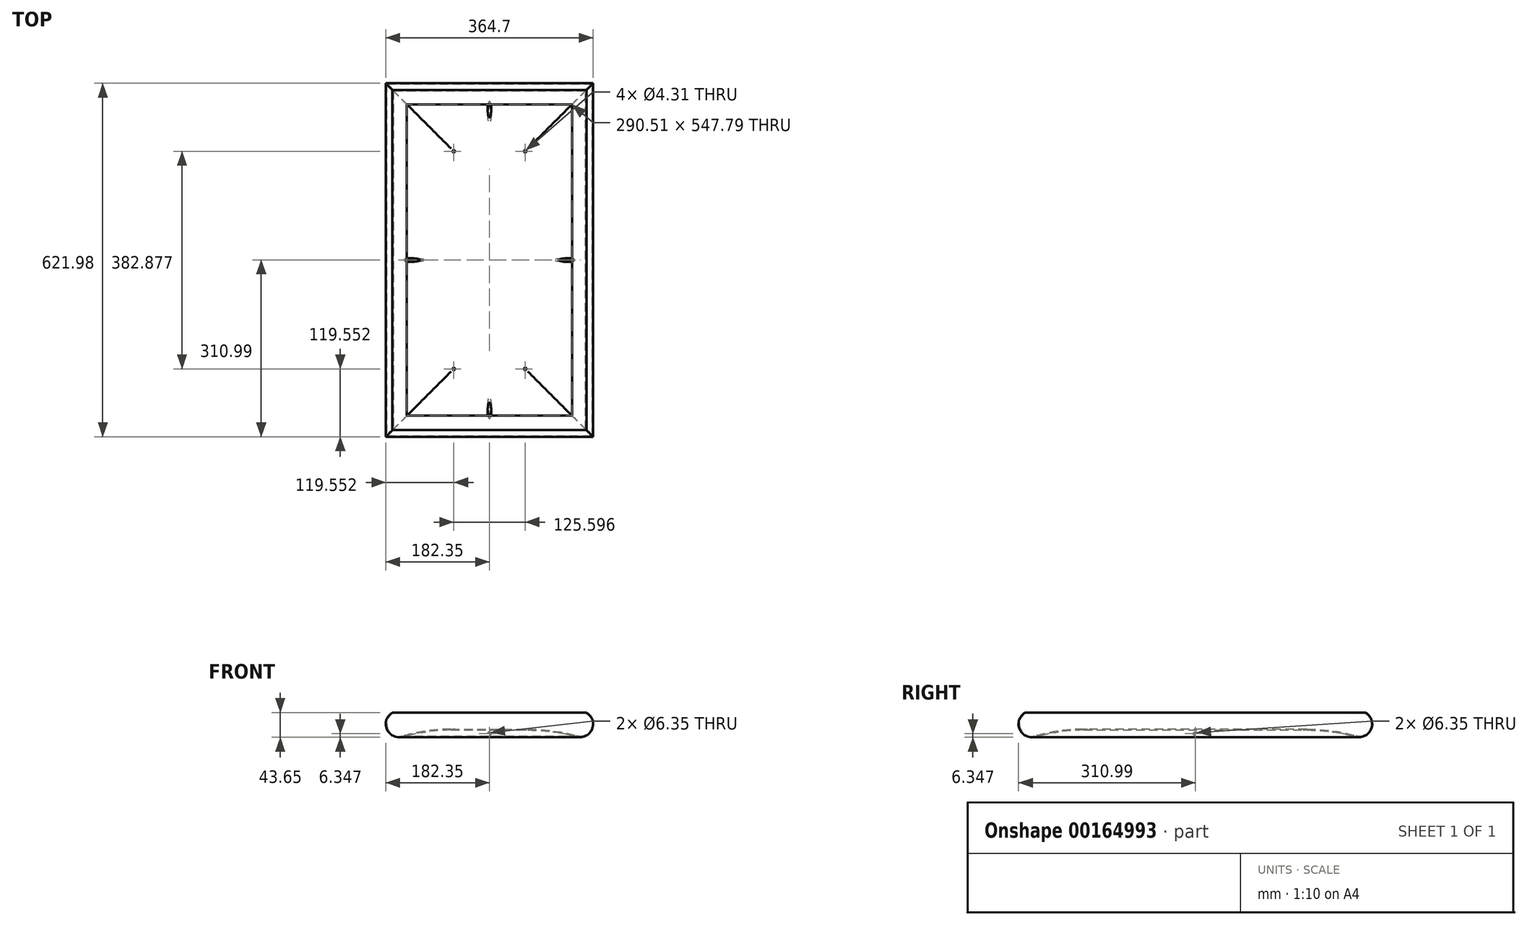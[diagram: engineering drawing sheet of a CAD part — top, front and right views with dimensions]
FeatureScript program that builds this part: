
annotation { "Feature Type Name" : "Feature", "Feature Type Description" : "" }
export const myFeature = defineFeature(function(context is Context, id is Id, definition is map)
    precondition{}
    {
        {
            var Q0;
            Q0=qCreatedBy(makeId("Top.planeOp"),FACE);
            var sketch = newSketch(context, id + "F0", { "sketchPlane" : qUnion([Q0])});
            skLineSegment(sketch, "E0.bottom", {"start": v(170.66, 299.3) * mm, "end": v(-170.66, 299.3) * mm});
            skLineSegment(sketch, "E0.top", {"start": v(170.66, -299.3) * mm, "end": v(-170.66, -299.3) * mm});
            skLineSegment(sketch, "E0.left", {"start": v(170.66, 299.3) * mm, "end": v(170.66, -299.3) * mm});
            skLineSegment(sketch, "E0.right", {"start": v(-170.66, 299.3) * mm, "end": v(-170.66, -299.3) * mm});
            skPoint(sketch, "E0.middle", {"position": v(0, 0) * mm});
            skSolve(sketch);
        }
        {
            var Q0;
            Q0=makeQuery(id+"F0.imprint","IMPRINT",FACE,{"disambiguationData":[TD([[makeQuery(id+"F0.imprint","IMPRINT",EDGE,{"derivedFrom":sQuery(id+"F0.wireOp",EDGE,"E0.bottom")}),1.0]])]});
            extrude(context, id + "F1", {"entities" : qUnion([Q0]), "depth" : 0.8 * mm});
        }
        {
            var Q0;
            Q0=makeQuery(id+"F1.opExtrude","SWEPT_FACE",FACE,{"disambiguationData":[OSD([sQuery(id+"F0.wireOp",EDGE,"E0.top")])]});
            var sketch = newSketch(context, id + "F2", { "sketchPlane" : qUnion([Q0])});
            skArc(sketch, "E1", {"start": v(152.58, -41.98) * mm, "mid": v(180.5, -28.57) * mm, "end": v(170.66, 0.8) * mm});
            skArc(sketch, "E2", {"start": v(153.01, -40.45) * mm, "mid": v(179.28, -27.4) * mm, "end": v(168.79, 0) * mm});
            skLineSegment(sketch, "E3", {"start": v(0, 0) * mm, "end": v(0, -28.57) * mm, "construction": true});
            skLineSegment(sketch, "E4.bottom", {"start": v(0, -28.57) * mm, "end": v(67.56, -28.57) * mm});
            skLineSegment(sketch, "E4.top", {"start": v(0, -30.16) * mm, "end": v(67.56, -30.16) * mm});
            skLineSegment(sketch, "E4.left", {"start": v(0, -28.57) * mm, "end": v(0, -30.16) * mm});
            skLineSegment(sketch, "E4.right", {"start": v(67.56, -28.58) * mm, "end": v(67.56, -30.16) * mm, "construction": true});
            skLineSegment(sketch, "E5", {"start": v(0, -30.16) * mm, "end": v(0, -42.86) * mm, "construction": true});
            skLineSegment(sketch, "E6", {"start": v(0, -42.86) * mm, "end": v(158.96, -42.86) * mm, "construction": true});
            skArc(sketch, "E7", {"start": v(153.01, -40.45) * mm, "mid": v(110.7, -31.56) * mm, "end": v(67.56, -28.58) * mm});
            skArc(sketch, "E8", {"start": v(152.58, -41.98) * mm, "mid": v(110.48, -33.13) * mm, "end": v(67.56, -30.16) * mm});
            skLineSegment(sketch, "E9", {"start": v(170.66, 0.8) * mm, "end": v(145.26, 15.46) * mm, "construction": true});
            skLineSegment(sketch, "E10", {"start": v(145.26, 15.46) * mm, "end": v(145.26, 0.8) * mm, "construction": true});
            skLineSegment(sketch, "E11", {"start": v(145.26, 0.8) * mm, "end": v(170.66, 0.8) * mm, "construction": true});
            skLineSegment(sketch, "E12", {"start": v(170.66, 0.8) * mm, "end": v(170.66, 0) * mm});
            skLineSegment(sketch, "E13", {"start": v(170.66, 0) * mm, "end": v(168.79, 0) * mm});
            skSolve(sketch);
        }
        {
            var Q0;
            Q0=makeQuery(id+"F2.imprint","IMPRINT",FACE,{"disambiguationData":[TD([[makeQuery(id+"F2.imprint","IMPRINT",EDGE,{"derivedFrom":sQuery(id+"F2.wireOp",EDGE,"E1")}),1.0]])]});
            var Q1;
            Q1=makeQuery(id+"F1.opExtrude","CAP_EDGE",EDGE,{"disambiguationData":[OSD([sQuery(id+"F0.wireOp",EDGE,"E0.left")])],"isStart":false});
            var Q2;
            Q2=makeQuery(id+"F1.opExtrude","CAP_EDGE",EDGE,{"disambiguationData":[OSD([sQuery(id+"F0.wireOp",EDGE,"E0.bottom")])],"isStart":false});
            var Q3;
            Q3=makeQuery(id+"F1.opExtrude","CAP_EDGE",EDGE,{"disambiguationData":[OSD([sQuery(id+"F0.wireOp",EDGE,"E0.right")])],"isStart":false});
            var Q4;
            Q4=makeQuery(id+"F1.opExtrude","CAP_EDGE",EDGE,{"disambiguationData":[OSD([sQuery(id+"F0.wireOp",EDGE,"E0.top")])],"isStart":false});
            sweep(context, id + "F3", {"operationType" : NewBodyOperationType.ADD, "profiles" : qUnion([Q0]), "path" : qUnion([Q1, Q2, Q3, Q4])});
        }
        {
            var Q0;
            Q0=makeQuery(id+"F1.opExtrude","CAP_FACE",FACE,{"disambiguationData":[OSD([sQuery(id+"F0.wireOp",EDGE,"E0.bottom"),sQuery(id+"F0.wireOp",EDGE,"E0.top"),sQuery(id+"F0.wireOp",EDGE,"E0.left"),sQuery(id+"F0.wireOp",EDGE,"E0.right")])],"isStart":false});
            var sketch = newSketch(context, id + "F4", { "sketchPlane" : qUnion([Q0])});
            skLineSegment(sketch, "E14.bottom", {"start": v(145.26, 273.9) * mm, "end": v(-145.26, 273.9) * mm});
            skLineSegment(sketch, "E14.top", {"start": v(145.26, -273.9) * mm, "end": v(-145.26, -273.9) * mm});
            skLineSegment(sketch, "E14.left", {"start": v(145.26, 273.9) * mm, "end": v(145.26, -273.9) * mm});
            skLineSegment(sketch, "E14.right", {"start": v(-145.26, 273.9) * mm, "end": v(-145.26, -273.9) * mm});
            skPoint(sketch, "E14.middle", {"position": v(0, 0) * mm});
            skLineSegment(sketch, "E15.bottom", {"start": v(145.26, 273.9) * mm, "end": v(170.66, 273.9) * mm, "construction": true});
            skLineSegment(sketch, "E15.top", {"start": v(145.26, 299.3) * mm, "end": v(170.66, 299.3) * mm, "construction": true});
            skLineSegment(sketch, "E15.left", {"start": v(145.26, 273.9) * mm, "end": v(145.26, 299.3) * mm, "construction": true});
            skLineSegment(sketch, "E15.right", {"start": v(170.66, 273.9) * mm, "end": v(170.66, 299.3) * mm, "construction": true});
            skSolve(sketch);
        }
        {
            var Q0;
            Q0=qSketchRegion(id+"F4",true);
            var Q1;
            Q1=makeQuery(id+"F1.opExtrude","CAP_FACE",FACE,{"disambiguationData":[OSD([sQuery(id+"F0.wireOp",EDGE,"E0.bottom"),sQuery(id+"F0.wireOp",EDGE,"E0.top"),sQuery(id+"F0.wireOp",EDGE,"E0.left"),sQuery(id+"F0.wireOp",EDGE,"E0.right")])],"isStart":true});
            extrude(context, id + "F5", {"entities" : qUnion([Q0]), "operationType" : NewBodyOperationType.REMOVE, "endBound" : BoundingType.UP_TO_SURFACE, "oppositeDirection" : true, "endBoundEntityFace" : qUnion([Q1]), "depth" : 25.4 * mm});
        }
        {
            var Q0;
            Q0=qCreatedBy(makeId("Front.planeOp"),FACE);
            var sketch = newSketch(context, id + "F6", { "sketchPlane" : qUnion([Q0])});
            skLineSegment(sketch, "E16", {"start": v(0, -30.16) * mm, "end": v(0, -36.51) * mm, "construction": true});
            skCircle(sketch, "E17", {"center": v(0, -36.51) * mm, "radius": 3.18 * mm});
            skSolve(sketch);
        }
        {
            var Q0;
            Q0=qSketchRegion(id+"F6",true);
            var Q1;
            Q1=makeQuery(id+"F3.opSweep","SWEPT_FACE",FACE,{"disambiguationData":[OSD([sQuery(id+"F0.wireOp",EDGE,"E0.bottom"),sQuery(id+"F2.wireOp",EDGE,"E2")])]});
            var Q2;
            Q2=makeQuery(id+"F3.opSweep","SWEPT_FACE",FACE,{"disambiguationData":[OSD([sQuery(id+"F0.wireOp",EDGE,"E0.top"),sQuery(id+"F2.wireOp",EDGE,"E2")])]});
            extrude(context, id + "F7", {"entities" : qUnion([Q0]), "operationType" : NewBodyOperationType.REMOVE, "endBound" : BoundingType.UP_TO_SURFACE, "oppositeDirection" : true, "endBoundEntityFace" : qUnion([Q1]), "depth" : 25.4 * mm, "hasSecondDirection" : true, "secondDirectionBound" : SecondDirectionBoundingType.UP_TO_SURFACE, "secondDirectionOppositeDirection" : false, "secondDirectionBoundEntityFace" : qUnion([Q2]), "secondDirectionDepth" : 25.4 * mm});
        }
        {
            var Q0;
            Q0=qCreatedBy(makeId("Right.planeOp"),FACE);
            var sketch = newSketch(context, id + "F8", { "sketchPlane" : qUnion([Q0])});
            skLineSegment(sketch, "E18", {"start": v(0, -30.16) * mm, "end": v(0, -36.51) * mm, "construction": true});
            skCircle(sketch, "E19", {"center": v(0, -36.51) * mm, "radius": 3.18 * mm});
            skSolve(sketch);
        }
        {
            var Q0;
            Q0=qSketchRegion(id+"F8",true);
            var Q1;
            Q1=makeQuery(id+"F3.opSweep","SWEPT_FACE",FACE,{"disambiguationData":[OSD([sQuery(id+"F0.wireOp",EDGE,"E0.right"),sQuery(id+"F2.wireOp",EDGE,"E2")])]});
            var Q2;
            Q2=makeQuery(id+"F3.opSweep","SWEPT_FACE",FACE,{"disambiguationData":[OSD([sQuery(id+"F0.wireOp",EDGE,"E0.left"),sQuery(id+"F2.wireOp",EDGE,"E2")])]});
            extrude(context, id + "F9", {"entities" : qUnion([Q0]), "operationType" : NewBodyOperationType.REMOVE, "endBound" : BoundingType.UP_TO_SURFACE, "oppositeDirection" : true, "endBoundEntityFace" : qUnion([Q1]), "depth" : 25.4 * mm, "hasSecondDirection" : true, "secondDirectionBound" : SecondDirectionBoundingType.UP_TO_SURFACE, "secondDirectionOppositeDirection" : false, "secondDirectionBoundEntityFace" : qUnion([Q2]), "secondDirectionDepth" : 25.4 * mm});
        }
        {
            var Q0;
            Q0=makeQuery(id+"F3.opSweep","SWEPT_FACE",FACE,{"disambiguationData":[OSD([sQuery(id+"F0.wireOp",EDGE,"E0.left"),sQuery(id+"F2.wireOp",EDGE,"E4.top")])]});
            var sketch = newSketch(context, id + "F10", { "sketchPlane" : qUnion([Q0])});
            skLineSegment(sketch, "E20", {"start": v(0, 196.2) * mm, "end": v(0, -196.2) * mm, "construction": true});
            skLineSegment(sketch, "E21.bottom", {"start": v(67.56, 196.2) * mm, "end": v(62.8, 196.2) * mm, "construction": true});
            skLineSegment(sketch, "E21.top", {"start": v(67.56, 191.44) * mm, "end": v(62.8, 191.44) * mm, "construction": true});
            skLineSegment(sketch, "E21.left", {"start": v(67.56, 196.2) * mm, "end": v(67.56, 191.44) * mm, "construction": true});
            skLineSegment(sketch, "E21.right", {"start": v(62.8, 196.2) * mm, "end": v(62.8, 191.44) * mm, "construction": true});
            skLineSegment(sketch, "E22.bottom", {"start": v(62.8, 191.44) * mm, "end": v(-62.8, 191.44) * mm, "construction": true});
            skLineSegment(sketch, "E22.top", {"start": v(62.8, -191.44) * mm, "end": v(-62.8, -191.44) * mm, "construction": true});
            skLineSegment(sketch, "E22.left", {"start": v(62.8, 191.44) * mm, "end": v(62.8, -191.44) * mm, "construction": true});
            skLineSegment(sketch, "E22.right", {"start": v(-62.8, 191.44) * mm, "end": v(-62.8, -191.44) * mm, "construction": true});
            skPoint(sketch, "E22.middle", {"position": v(0, 0) * mm});
            skCircle(sketch, "E23", {"center": v(-62.8, 191.44) * mm, "radius": 2.15 * mm});
            skCircle(sketch, "E24", {"center": v(62.8, 191.44) * mm, "radius": 2.15 * mm});
            skCircle(sketch, "E25", {"center": v(62.8, -191.44) * mm, "radius": 2.15 * mm});
            skCircle(sketch, "E26", {"center": v(-62.8, -191.44) * mm, "radius": 2.15 * mm});
            skSolve(sketch);
        }
        {
            var Q0;
            Q0=qSketchRegion(id+"F10",true);
            var Q1;
            Q1=makeQuery(id+"F3.opSweep","SWEPT_FACE",FACE,{"disambiguationData":[OSD([sQuery(id+"F0.wireOp",EDGE,"E0.left"),sQuery(id+"F2.wireOp",EDGE,"E4.bottom")])]});
            extrude(context, id + "F11", {"entities" : qUnion([Q0]), "operationType" : NewBodyOperationType.REMOVE, "endBound" : BoundingType.UP_TO_SURFACE, "oppositeDirection" : true, "endBoundEntityFace" : qUnion([Q1]), "depth" : 25.4 * mm});
        }
    });
